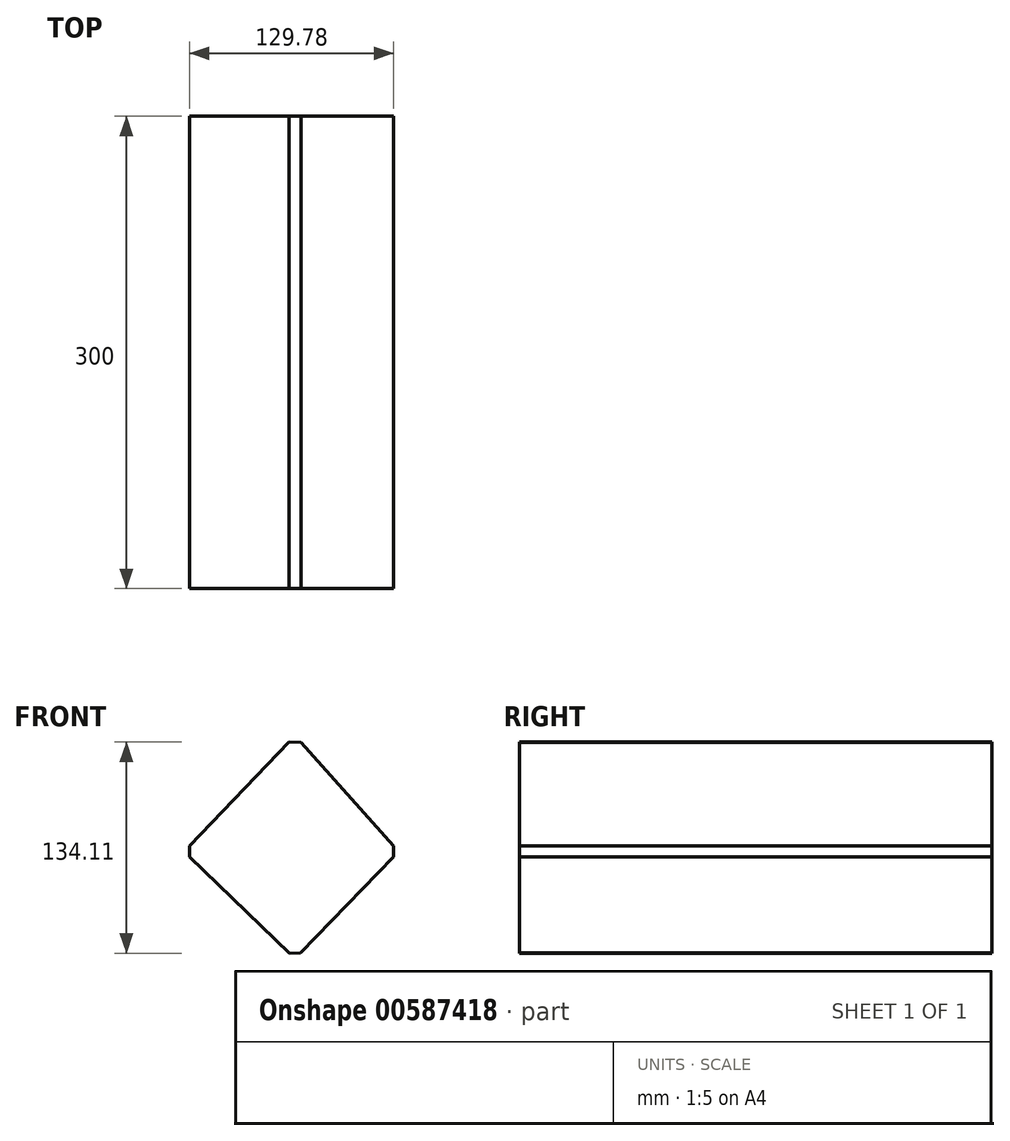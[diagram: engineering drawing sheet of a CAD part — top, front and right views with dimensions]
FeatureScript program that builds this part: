
annotation { "Feature Type Name" : "Feature", "Feature Type Description" : "" }
export const myFeature = defineFeature(function(context is Context, id is Id, definition is map)
    precondition{}
    {
        {
            var Q0;
            Q0=qCreatedBy(makeId("Front.planeOp"),FACE);
            var sketch = newSketch(context, id + "F0", { "sketchPlane" : qUnion([Q0])});
            skLineSegment(sketch, "E0", {"start": v(0, 73.4) * mm, "end": v(-70.74, 0) * mm});
            skLineSegment(sketch, "E1", {"start": v(-70.74, 0) * mm, "end": v(0, -68.18) * mm});
            skLineSegment(sketch, "E2", {"start": v(0, -68.18) * mm, "end": v(65.7, 0) * mm});
            skLineSegment(sketch, "E3", {"start": v(65.7, 0) * mm, "end": v(0, 73.4) * mm});
            skSolve(sketch);
        }
        {
            var Q0;
            Q0 = qSketchRegion(id + "F0", true);
            extrude(context, id + "F1", {"entities" : qUnion([Q0]), "depth" : 300 * mm, "offsetDistance" : 25.4 * mm});
        }
        {
            var Q0;
            Q0=makeQuery(id+"F1.opExtrude","SWEPT_EDGE",EDGE,{"disambiguationData":[OSD([sQuery(id+"F0.wireOp",EDGE,"E0"),sQuery(id+"F0.wireOp",EDGE,"E3")])]});
            var Q1;
            Q1=makeQuery(id+"F1.opExtrude","SWEPT_EDGE",EDGE,{"disambiguationData":[OSD([sQuery(id+"F0.wireOp",EDGE,"E0"),sQuery(id+"F0.wireOp",EDGE,"E1")])]});
            var Q2;
            Q2=makeQuery(id+"F1.opExtrude","SWEPT_EDGE",EDGE,{"disambiguationData":[OSD([sQuery(id+"F0.wireOp",EDGE,"E2"),sQuery(id+"F0.wireOp",EDGE,"E3")])]});
            var Q3;
            Q3=makeQuery(id+"F1.opExtrude","SWEPT_EDGE",EDGE,{"disambiguationData":[OSD([sQuery(id+"F0.wireOp",EDGE,"E1"),sQuery(id+"F0.wireOp",EDGE,"E2")])]});
            chamfer(context, id + "F2", {"entities" : qUnion([Q0, Q1, Q2, Q3]), "width" : 5.08 * mm, "tangentPropagation" : true});
        }
    });
